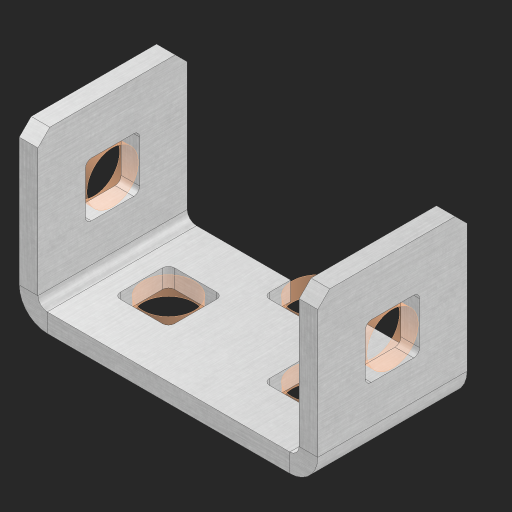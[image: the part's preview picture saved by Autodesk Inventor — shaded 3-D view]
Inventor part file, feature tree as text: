
AUTODESK INVENTOR PART (.ipt)
format: ipt  version: 2023 (Build 270158000, 158)  size: 559,616 bytes
history: native  units: in
note: dims shown in document units (in); Inventor stores cm internally (conversion verified against a paired STEP export)
features: other x45, extrude x36, sheet_metal_op x11, sketch x10, pattern_linear x2, mirror x1, chamfer x1
ambient origin geometry x8: Origin, YZ Plane, XZ Plane, XY Plane, X Axis, Y Axis, Z Axis, Center Point
bodies: Solid1 (feature_tree), Body (feature_tree)
feature tree (106):
  sheet_metal_op  "Flanges"
  other  "Flange Pattern Plane"
  other  "Flange Pattern Sketch"
  sheet_metal_op  "Flange Pattern"
  sheet_metal_op  "Body Pattern"
  pattern_linear  "Center Pattern"  Spacing1=0.0625in  [1 undecoded]
  other  "Arc Length"
  mirror  "Notch Mirror"
  pattern_linear  "Notch Pattern"  Spacing1=0.182in  [1 undecoded]
  chamfer  "End Chamfer"
  extrude  "Half Cut"  Depth=0.02in
  sketch  "Sketch1"  dims[d0=1.0in]
  other  "Plate1"
  sketch  "Sketch2"  dims[d1=0.5in]
  other  "Plate2"
  sheet_metal_op  "Bend1"
  sheet_metal_op  "Corner1"
  sketch  "Sketch3"  dims[d2=0.0625in]
  sketch  "Sketch7"  dims[d3=0.0625in]
  other  "Srf1"
  other  "Srf2"
  sketch  "Sketch8"  dims[d4=0.0312in]
  sketch  "Sketch9"  dims[d5=0.125in]
  other  "Srf91"
  sheet_metal_op  "Body Pattern Sketch"
  other  "Srf92"
  sketch  "Sketch13"  dims[d6=0.0625in]
  sketch  "Sketch14"  dims[d7=0.5in d8=90.0deg d9=0.0312in]
  sketch  "Sketch15"  dims[d10=0.25in]
  sketch  "Sketch16"  dims[d11=0.0625in d12=0.0625in d16=0.182in d17=0.02in d18=0.0625in d19=0.0in d20=0.25in d21=0.25in d38=0.3937in d40=0.5in d41=0.7874in d43=1.0in d46=0.172in d47=1.0in d48=0.0in d49=0.182in d50=0.02in d51=0.25in d52=0.25in d53=0.0625in d54=0.0in d55=0.172in d56=1.0in d57=0.0in d58=0.25in d60=0.3937in d62=0.5in d63=0.7874in d65=0.5in d85=0.1473in d86=0.1782in d88=0.04in d89=0.0625in d90=0.0in d91=0.04in d92=0.0491in d95=2.5in d96=0.04in d97=0.25in d98=45.0deg d99=0.25in d100=0.5in d101=0.0in d102=2.497in d106=0.182in d107=0.02in d108=0.5in d109=0.5in d110=0.0625in d111=0.0in d112=0.172in d113=0.5in d114=0.0in d117=0.5in d118=0.5in d119=0.5in]
  other  "Srf786"
  other  "Srf889"
  other  "Srf890"
  other  "Srf891"
  other  "Srf892"
  other  "Srf893"
  other  "Srf894"
  other  "Srf895"
  other  "Srf896"
  other  "Srf996"
  other  "Srf997"
  other  "Srf998"
  other  "Srf999"
  other  "Srf1000"
  other  "Srf1255"
  other  "Srf1256"
  other  "Srf1257"
  other  "Srf1258"
  other  "Srf1259"
  other  "Srf1260"
  other  "Srf1261"
  other  "Srf1262"
  other  "Srf1263"
  other  "Srf1264"
  other  "Srf1265"
  other  "Srf1266"
  other  "Srf1267"
  other  "Srf1268"
  other  "Srf1269"
  other  "Srf1270"
  other  "Srf1271"
  other  "Srf1272"
  other  "Srf1273"
  other  "Srf1274"
  sheet_metal_op  "Flange Stamp"
  sheet_metal_op  "Flange Circle"
  sheet_metal_op  "Body Stamp"
  sheet_metal_op  "Body Circle"
  other  "Center Stamp"
  other  "Center Circle"
  sheet_metal_op  "Notch"
  extrude  "ExtrusionSrf2"  Depth=0.0625in
  extrude  "ExtrusionSrf92"  TaperAngle=0.0deg  [1 undecoded]
  extrude  "ExtrusionSrf889"  Depth=0.25in
  extrude  "ExtrusionSrf890"  Depth=0.25in
  extrude  "ExtrusionSrf891"  Depth=0.3937in
  extrude  "ExtrusionSrf892"  Depth=0.5in
  extrude  "ExtrusionSrf893"  Depth=1.0in TaperAngle=0.0deg
  extrude  "ExtrusionSrf894"  Depth=0.182in
  extrude  "ExtrusionSrf895"  Depth=0.02in
  extrude  "ExtrusionSrf896"  Depth=0.25in
  extrude  "ExtrusionSrf996"  Depth=0.25in
  extrude  "ExtrusionSrf997"  Depth=0.0625in
  extrude  "ExtrusionSrf998"  TaperAngle=0.0deg  [1 undecoded]
  extrude  "ExtrusionSrf999"  Depth=0.5in
  extrude  "ExtrusionSrf1000"  Depth=1.0in TaperAngle=0.0deg
  extrude  "ExtrusionSrf1255"  Depth=0.25in
  extrude  "ExtrusionSrf1256"  Depth=0.3937in
  extrude  "ExtrusionSrf1257"  Depth=0.5in
  extrude  "ExtrusionSrf1258"  Depth=0.5in
  extrude  "ExtrusionSrf1259"  Depth=0.5in
  extrude  "ExtrusionSrf1260"  Depth=0.5in
  extrude  "ExtrusionSrf1261"  Depth=0.0625in
  extrude  "ExtrusionSrf1262"  TaperAngle=0.0deg  [1 undecoded]
  extrude  "ExtrusionSrf1263"  Depth=0.5in
  extrude  "ExtrusionSrf1264"  Depth=0.5in
  extrude  "ExtrusionSrf1265"  Depth=0.5in
  extrude  "ExtrusionSrf1266"  Depth=0.25in TaperAngle=45.0deg
  extrude  "ExtrusionSrf1267"  Depth=0.25in
  extrude  "ExtrusionSrf1268"  Depth=0.5in TaperAngle=0.0deg
  extrude  "ExtrusionSrf1269"  Depth=0.5in
  extrude  "ExtrusionSrf1270"  Depth=0.182in
  extrude  "ExtrusionSrf1271"  Depth=0.02in
  extrude  "ExtrusionSrf1272"  Depth=0.5in
  extrude  "ExtrusionSrf1273"  Depth=0.5in
  extrude  "ExtrusionSrf1274"  Depth=0.0625in
note: 5 required parameter values undecoded (feature->parameter linkage not recoverable at this tier; creation-order binding heuristic only, values carry confidence <= 0.55)
